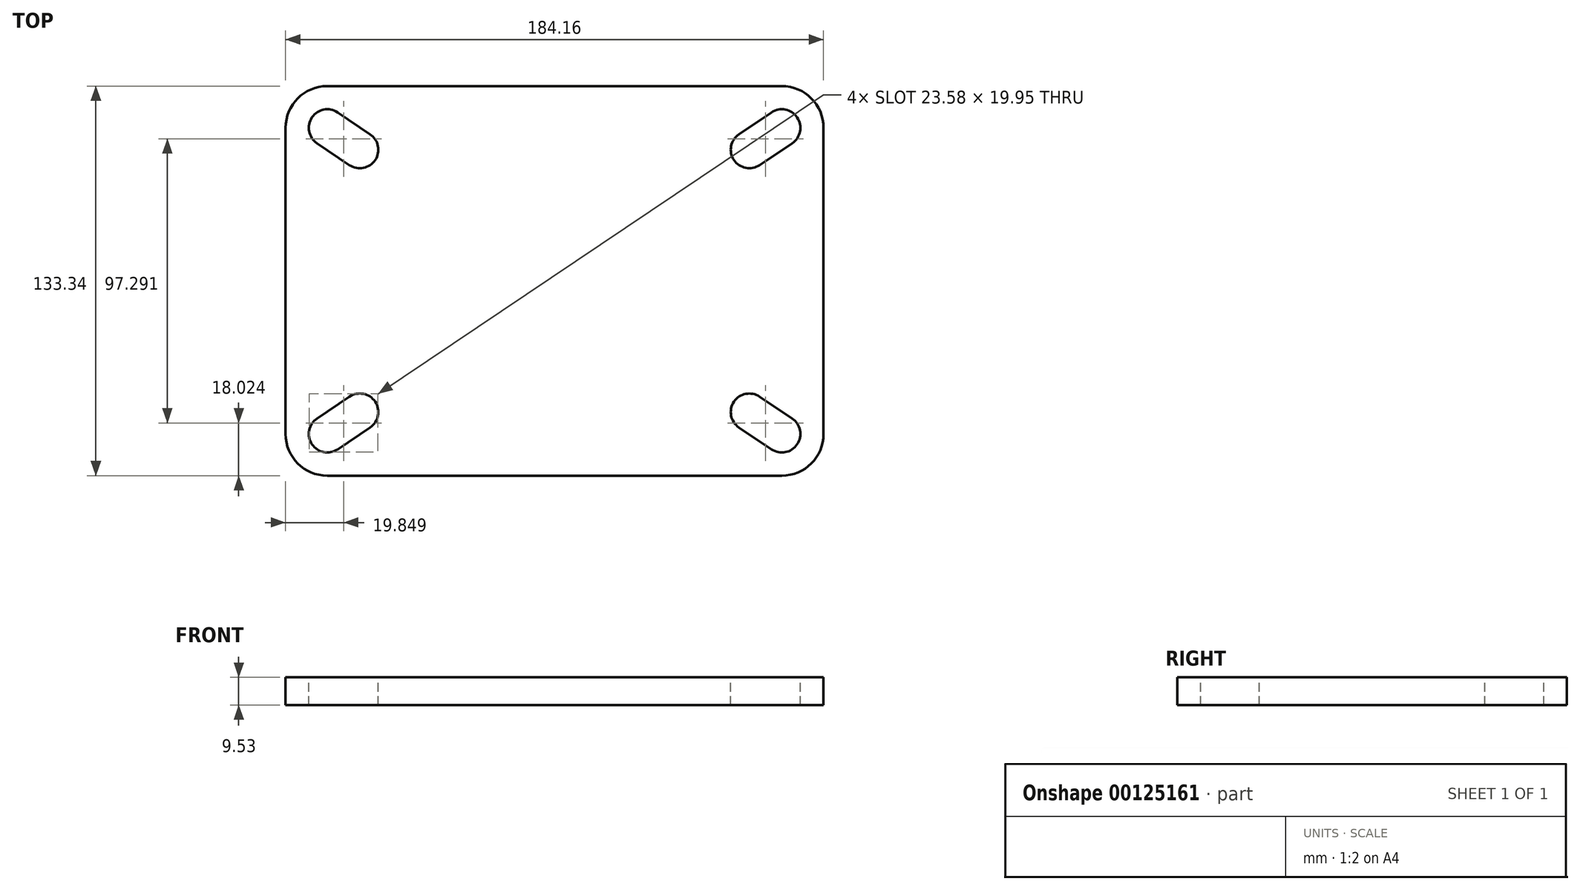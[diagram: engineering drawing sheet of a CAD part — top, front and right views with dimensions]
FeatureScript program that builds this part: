
annotation { "Feature Type Name" : "Feature", "Feature Type Description" : "" }
export const myFeature = defineFeature(function(context is Context, id is Id, definition is map)
    precondition{}
    {
        {
            var Q0;
            Q0=qCreatedBy(makeId("Top.planeOp"),FACE);
            var sketch = newSketch(context, id + "F0", { "sketchPlane" : qUnion([Q0])});
            skLineSegment(sketch, "E0.bottom", {"start": v(77.79, -66.68) * mm, "end": v(-77.79, -66.68) * mm});
            skLineSegment(sketch, "E0.top", {"start": v(77.79, 66.68) * mm, "end": v(-77.79, 66.68) * mm});
            skLineSegment(sketch, "E0.left", {"start": v(92.08, -52.39) * mm, "end": v(92.08, 52.39) * mm});
            skLineSegment(sketch, "E0.right", {"start": v(-92.08, -52.39) * mm, "end": v(-92.08, 52.39) * mm});
            skPoint(sketch, "E0.middle", {"position": v(0, 0) * mm});
            skArc(sketch, "E1", {"start": v(-77.79, 66.68) * mm, "mid": v(-87.9, 62.5) * mm, "end": v(-92.08, 52.39) * mm});
            skArc(sketch, "E2", {"start": v(92.07, 52.39) * mm, "mid": v(87.9, 62.5) * mm, "end": v(77.79, 66.68) * mm});
            skArc(sketch, "E3", {"start": v(-92.07, -52.39) * mm, "mid": v(-87.9, -62.5) * mm, "end": v(-77.79, -66.67) * mm});
            skArc(sketch, "E4", {"start": v(77.79, -66.67) * mm, "mid": v(87.9, -62.5) * mm, "end": v(92.08, -52.39) * mm});
            skPoint(sketch, "E5.orphan", {"position": v(92.08, 66.68) * mm});
            skPoint(sketch, "E6.orphan", {"position": v(92.08, -66.68) * mm});
            skPoint(sketch, "E7.orphan", {"position": v(-92.08, -66.68) * mm});
            skPoint(sketch, "E8.orphan", {"position": v(-92.08, 66.68) * mm});
            skArc(sketch, "E9", {"start": v(-74.24, 57.65) * mm, "mid": v(-83.05, 55.93) * mm, "end": v(-81.33, 47.12) * mm});
            skArc(sketch, "E10", {"start": v(81.33, 47.12) * mm, "mid": v(83.05, 55.93) * mm, "end": v(74.24, 57.65) * mm});
            skArc(sketch, "E11", {"start": v(74.24, -57.65) * mm, "mid": v(83.05, -55.93) * mm, "end": v(81.33, -47.12) * mm});
            skArc(sketch, "E12", {"start": v(-81.33, -47.12) * mm, "mid": v(-83.05, -55.93) * mm, "end": v(-74.24, -57.65) * mm});
            skArc(sketch, "E13", {"start": v(-70.22, 39.64) * mm, "mid": v(-61.4, 41.36) * mm, "end": v(-63.13, 50.17) * mm});
            skArc(sketch, "E14", {"start": v(63.13, 50.17) * mm, "mid": v(61.4, 41.36) * mm, "end": v(70.22, 39.64) * mm});
            skArc(sketch, "E15", {"start": v(-63.13, -50.17) * mm, "mid": v(-61.4, -41.36) * mm, "end": v(-70.22, -39.64) * mm});
            skArc(sketch, "E16", {"start": v(70.22, -39.64) * mm, "mid": v(61.4, -41.36) * mm, "end": v(63.13, -50.17) * mm});
            skLineSegment(sketch, "E17", {"start": v(-74.24, 57.65) * mm, "end": v(-63.13, 50.17) * mm});
            skLineSegment(sketch, "E18", {"start": v(-81.33, 47.12) * mm, "end": v(-70.22, 39.64) * mm});
            skLineSegment(sketch, "E19", {"start": v(63.13, 50.17) * mm, "end": v(74.24, 57.65) * mm});
            skLineSegment(sketch, "E20", {"start": v(70.22, 39.64) * mm, "end": v(81.33, 47.12) * mm});
            skLineSegment(sketch, "E21", {"start": v(70.22, -39.64) * mm, "end": v(81.33, -47.12) * mm});
            skLineSegment(sketch, "E22", {"start": v(63.13, -50.17) * mm, "end": v(74.24, -57.65) * mm});
            skLineSegment(sketch, "E23", {"start": v(-74.24, -57.65) * mm, "end": v(-63.13, -50.17) * mm});
            skLineSegment(sketch, "E24", {"start": v(-81.33, -47.12) * mm, "end": v(-70.22, -39.64) * mm});
            skSolve(sketch);
        }
        {
            var Q0;
            Q0=qSketchRegion(id+"F0",true);
            extrude(context, id + "F1", {"entities" : qUnion([Q0]), "oppositeDirection" : true, "depth" : 9.52 * mm});
        }
    });
